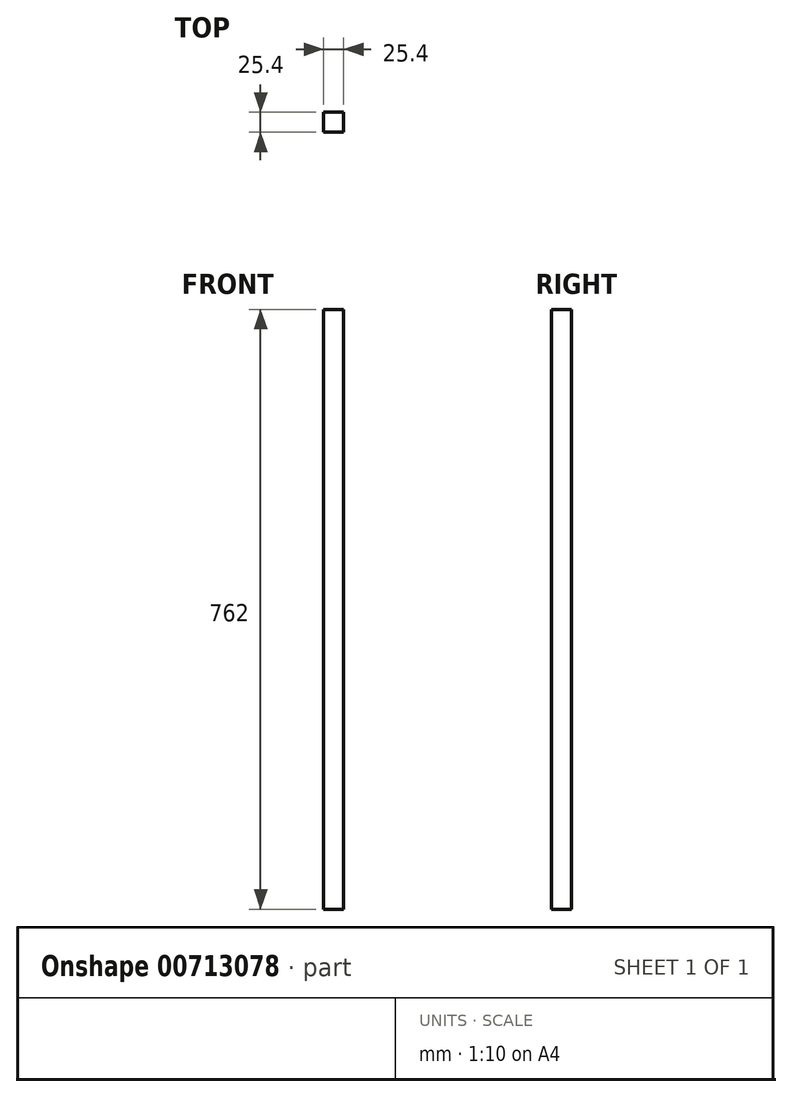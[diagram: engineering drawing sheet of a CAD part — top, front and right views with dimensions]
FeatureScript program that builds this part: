
annotation { "Feature Type Name" : "Feature", "Feature Type Description" : "" }
export const myFeature = defineFeature(function(context is Context, id is Id, definition is map)
    precondition{}
    {
        {
            var Q0;
            Q0=qCreatedBy(makeId("Top.planeOp"),FACE);
            var sketch = newSketch(context, id + "F0", { "sketchPlane" : qUnion([Q0])});
            skLineSegment(sketch, "E0.bottom", {"start": v(12.7, -12.7) * mm, "end": v(-12.7, -12.7) * mm});
            skLineSegment(sketch, "E0.top", {"start": v(12.7, 12.7) * mm, "end": v(-12.7, 12.7) * mm});
            skLineSegment(sketch, "E0.left", {"start": v(12.7, -12.7) * mm, "end": v(12.7, 12.7) * mm});
            skLineSegment(sketch, "E0.right", {"start": v(-12.7, -12.7) * mm, "end": v(-12.7, 12.7) * mm});
            skPoint(sketch, "E0.middle", {"position": v(0, 0) * mm});
            skSolve(sketch);
        }
        {
            var Q0;
            Q0=makeQuery(id+"F0.imprint","IMPRINT",FACE,{"disambiguationData":[TD([[makeQuery(id+"F0.imprint","IMPRINT",EDGE,{"derivedFrom":sQuery(id+"F0.wireOp",EDGE,"E0.bottom")}),-1.0]])]});
            extrude(context, id + "F1", {"entities" : qUnion([Q0]), "depth" : 762 * mm});
        }
    });
